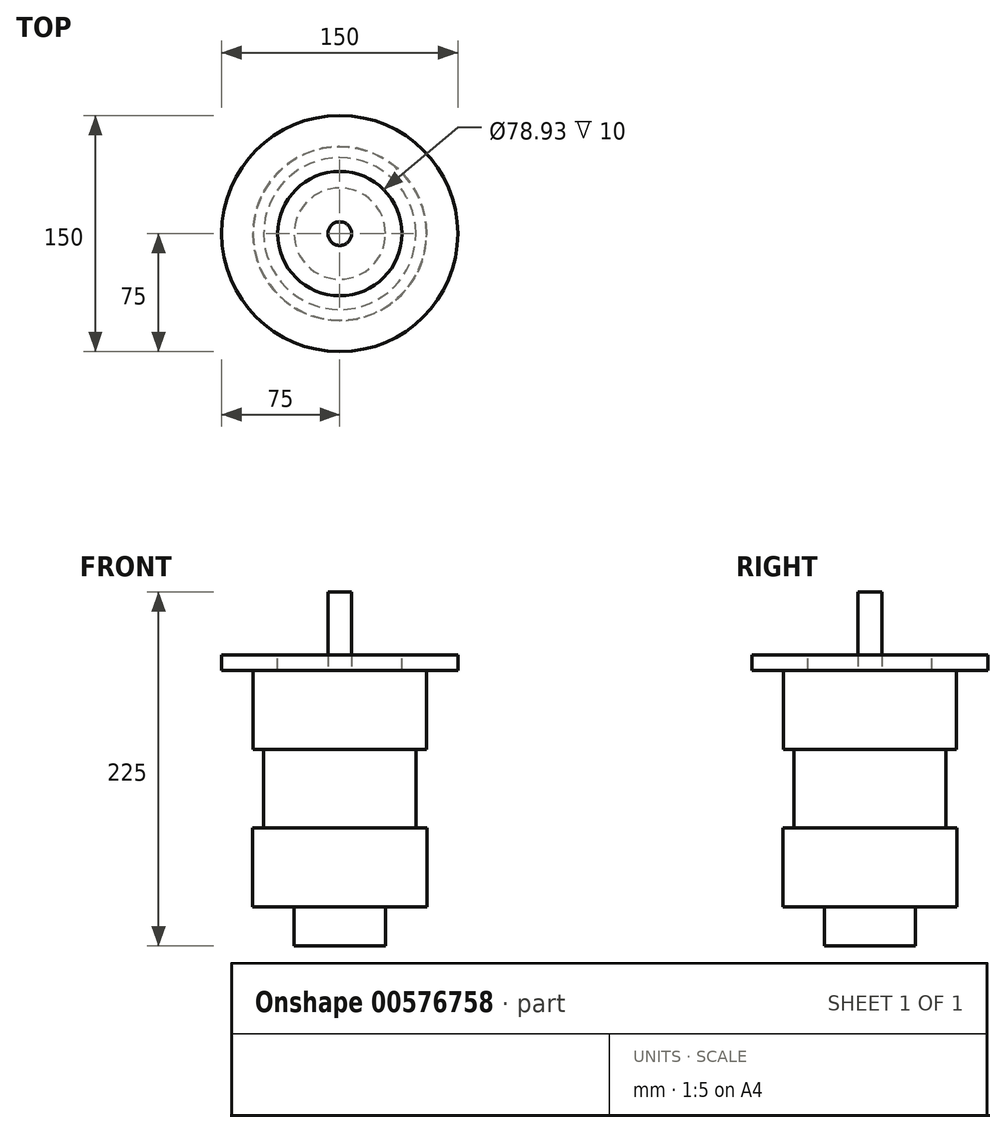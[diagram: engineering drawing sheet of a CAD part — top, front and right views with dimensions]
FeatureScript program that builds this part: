
annotation { "Feature Type Name" : "Feature", "Feature Type Description" : "" }
export const myFeature = defineFeature(function(context is Context, id is Id, definition is map)
    precondition{}
    {
        {
            var Q0;
            Q0=qCreatedBy(makeId("Top.planeOp"),FACE);
            var sketch = newSketch(context, id + "F0", { "sketchPlane" : qUnion([Q0])});
            skCircle(sketch, "E0", {"center": v(0, 0) * mm, "radius": 55 * mm});
            skSolve(sketch);
        }
        {
            var Q0;
            Q0 = qSketchRegion(id + "F0", true);
            extrude(context, id + "F1", {"entities" : qUnion([Q0]), "depth" : 50 * mm, "offsetDistance" : 25 * mm});
        }
        {
            var Q0;
            Q0=makeQuery(id+"F1.opExtrude","CAP_FACE",FACE,{"disambiguationData":[OSD([sQuery(id+"F0.wireOp",EDGE,"E0")])],"isStart":false});
            var sketch = newSketch(context, id + "F2", { "sketchPlane" : qUnion([Q0])});
            skCircle(sketch, "E1", {"center": v(0, 0) * mm, "radius": 75 * mm});
            skSolve(sketch);
        }
        {
            var Q0;
            Q0 = qSketchRegion(id + "F2", true);
            extrude(context, id + "F3", {"entities" : qUnion([Q0]), "operationType" : NewBodyOperationType.ADD, "depth" : 10 * mm, "offsetDistance" : 25 * mm});
        }
        {
            var Q0;
            Q0=makeQuery(id+"F1.opExtrude","CAP_FACE",FACE,{"disambiguationData":[OSD([sQuery(id+"F0.wireOp",EDGE,"E0")])],"isStart":true});
            var sketch = newSketch(context, id + "F4", { "sketchPlane" : qUnion([Q0])});
            skCircle(sketch, "E2", {"center": v(0, 0) * mm, "radius": 48.29 * mm});
            skSolve(sketch);
        }
        {
            var Q0;
            Q0 = qSketchRegion(id + "F4", true);
            extrude(context, id + "F5", {"entities" : qUnion([Q0]), "operationType" : NewBodyOperationType.ADD, "depth" : 50 * mm, "offsetDistance" : 25 * mm});
        }
        {
            var Q0;
            Q0=makeQuery(id+"F5.opExtrude","CAP_FACE",FACE,{"disambiguationData":[OSD([sQuery(id+"F4.wireOp",EDGE,"E2")])],"isStart":false});
            var sketch = newSketch(context, id + "F6", { "sketchPlane" : qUnion([Q0])});
            skCircle(sketch, "E3", {"center": v(0, 0) * mm, "radius": 55.3 * mm});
            skSolve(sketch);
        }
        {
            var Q0;
            Q0 = qSketchRegion(id + "F6", true);
            extrude(context, id + "F7", {"entities" : qUnion([Q0]), "operationType" : NewBodyOperationType.ADD, "depth" : 50 * mm, "offsetDistance" : 25 * mm});
        }
        {
            var Q0;
            Q0=makeQuery(id+"F3.opExtrude","CAP_FACE",FACE,{"disambiguationData":[OSD([sQuery(id+"F2.wireOp",EDGE,"E1")])],"isStart":false});
            var sketch = newSketch(context, id + "F8", { "sketchPlane" : qUnion([Q0])});
            skCircle(sketch, "E4", {"center": v(0, 0) * mm, "radius": 39.47 * mm});
            skSolve(sketch);
        }
        {
            var Q0;
            Q0 = qSketchRegion(id + "F8", true);
            extrude(context, id + "F9", {"entities" : qUnion([Q0]), "operationType" : NewBodyOperationType.REMOVE, "oppositeDirection" : true, "depth" : 10 * mm, "offsetDistance" : 25 * mm});
        }
        {
            var Q0;
            Q0=makeQuery(id+"F9.boolean.opBoolean","COPY",FACE,{"derivedFrom":makeQuery(id+"F9.opExtrude","CAP_FACE",FACE,{"disambiguationData":[OSD([sQuery(id+"F8.wireOp",EDGE,"E4")])],"isStart":false})});
            var sketch = newSketch(context, id + "F10", { "sketchPlane" : qUnion([Q0])});
            skCircle(sketch, "E5", {"center": v(0, 0) * mm, "radius": 7.5 * mm});
            skSolve(sketch);
        }
        {
            var Q0;
            Q0 = qSketchRegion(id + "F10", true);
            extrude(context, id + "F11", {"entities" : qUnion([Q0]), "operationType" : NewBodyOperationType.ADD, "depth" : 50 * mm, "offsetDistance" : 25 * mm});
        }
        {
            var Q0;
            Q0=makeQuery(id+"F7.opExtrude","CAP_FACE",FACE,{"disambiguationData":[OSD([sQuery(id+"F6.wireOp",EDGE,"E3")])],"isStart":false});
            var sketch = newSketch(context, id + "F12", { "sketchPlane" : qUnion([Q0])});
            skCircle(sketch, "E6", {"center": v(0, 0) * mm, "radius": 29 * mm});
            skSolve(sketch);
        }
        {
            var Q0;
            Q0 = qSketchRegion(id + "F12", true);
            extrude(context, id + "F13", {"entities" : qUnion([Q0]), "operationType" : NewBodyOperationType.ADD, "depth" : 25 * mm, "offsetDistance" : 25 * mm});
        }
    });
